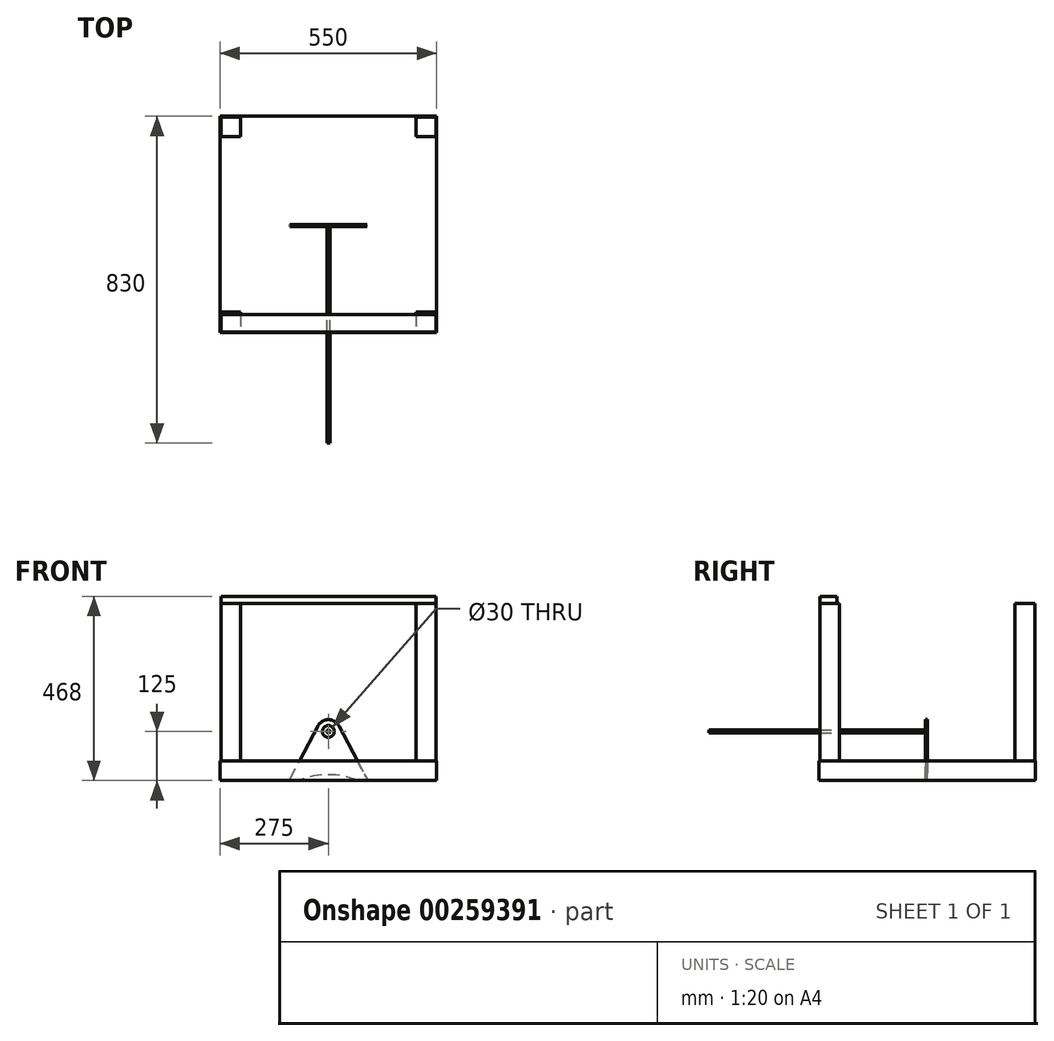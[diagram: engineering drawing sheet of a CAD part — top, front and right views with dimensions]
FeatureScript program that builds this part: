
annotation { "Feature Type Name" : "Feature", "Feature Type Description" : "" }
export const myFeature = defineFeature(function(context is Context, id is Id, definition is map)
    precondition{}
    {
        {
            var Q0;
            Q0=qCreatedBy(makeId("Top.planeOp"),FACE);
            var sketch = newSketch(context, id + "F0", { "sketchPlane" : qUnion([Q0])});
            skLineSegment(sketch, "E0.bottom", {"start": v(-275, 275) * mm, "end": v(275, 275) * mm});
            skLineSegment(sketch, "E0.top", {"start": v(-275, -275) * mm, "end": v(275, -275) * mm});
            skLineSegment(sketch, "E0.left", {"start": v(-275, 275) * mm, "end": v(-275, -275) * mm});
            skLineSegment(sketch, "E0.right", {"start": v(275, 275) * mm, "end": v(275, -275) * mm});
            skLineSegment(sketch, "E1.bottom", {"start": v(-273, -223) * mm, "end": v(-223, -223) * mm});
            skLineSegment(sketch, "E1.top", {"start": v(-273, -273) * mm, "end": v(-223, -273) * mm});
            skLineSegment(sketch, "E1.left", {"start": v(-273, -223) * mm, "end": v(-273, -273) * mm});
            skLineSegment(sketch, "E1.right", {"start": v(-223, -223) * mm, "end": v(-223, -273) * mm});
            skLineSegment(sketch, "E2.bottom", {"start": v(-273, 273) * mm, "end": v(-223, 273) * mm});
            skLineSegment(sketch, "E2.top", {"start": v(-273, 223) * mm, "end": v(-223, 223) * mm});
            skLineSegment(sketch, "E2.left", {"start": v(-273, 273) * mm, "end": v(-273, 223) * mm});
            skLineSegment(sketch, "E2.right", {"start": v(-223, 273) * mm, "end": v(-223, 223) * mm});
            skLineSegment(sketch, "E3.bottom", {"start": v(223, 273) * mm, "end": v(273, 273) * mm});
            skLineSegment(sketch, "E3.top", {"start": v(223, 223) * mm, "end": v(273, 223) * mm});
            skLineSegment(sketch, "E3.left", {"start": v(223, 273) * mm, "end": v(223, 223) * mm});
            skLineSegment(sketch, "E3.right", {"start": v(273, 273) * mm, "end": v(273, 223) * mm});
            skLineSegment(sketch, "E4.bottom", {"start": v(223, -223) * mm, "end": v(273, -223) * mm});
            skLineSegment(sketch, "E4.top", {"start": v(223, -273) * mm, "end": v(273, -273) * mm});
            skLineSegment(sketch, "E4.left", {"start": v(223, -223) * mm, "end": v(223, -273) * mm});
            skLineSegment(sketch, "E4.right", {"start": v(273, -223) * mm, "end": v(273, -273) * mm});
            skSolve(sketch);
        }
        {
            var Q0;
            Q0 = qSketchRegion(id + "F0", true);
            extrude(context, id + "F1", {"entities" : qUnion([Q0]), "depth" : 50 * mm});
        }
        {
            var Q0;
            Q0=makeQuery(id+"F0.imprint","IMPRINT",FACE,{"disambiguationData":[TD([[makeQuery(id+"F0.imprint","IMPRINT",EDGE,{"derivedFrom":sQuery(id+"F0.wireOp",EDGE,"E2.bottom")}),-1.0]])]});
            var Q1;
            Q1=makeQuery(id+"F0.imprint","IMPRINT",FACE,{"disambiguationData":[TD([[makeQuery(id+"F0.imprint","IMPRINT",EDGE,{"derivedFrom":sQuery(id+"F0.wireOp",EDGE,"E3.bottom")}),-1.0]])]});
            var Q2;
            Q2=makeQuery(id+"F0.imprint","IMPRINT",FACE,{"disambiguationData":[TD([[makeQuery(id+"F0.imprint","IMPRINT",EDGE,{"derivedFrom":sQuery(id+"F0.wireOp",EDGE,"E4.bottom")}),-1.0]])]});
            var Q3;
            Q3=makeQuery(id+"F0.imprint","IMPRINT",FACE,{"disambiguationData":[TD([[makeQuery(id+"F0.imprint","IMPRINT",EDGE,{"derivedFrom":sQuery(id+"F0.wireOp",EDGE,"E1.bottom")}),-1.0]])]});
            extrude(context, id + "F2", {"entities" : qUnion([Q0, Q1, Q2, Q3]), "operationType" : NewBodyOperationType.ADD, "depth" : 450 * mm});
        }
        {
            var Q0;
            Q0=makeQuery(id+"F2.opExtrude","SWEPT_FACE",FACE,{"disambiguationData":[OSD([sQuery(id+"F0.wireOp",EDGE,"E4.right")])]});
            var sketch = newSketch(context, id + "F3", { "sketchPlane" : qUnion([Q0])});
            skLineSegment(sketch, "E5.bottom", {"start": v(-273, 450) * mm, "end": v(-229, 450) * mm});
            skLineSegment(sketch, "E5.top", {"start": v(-273, 468) * mm, "end": v(-229, 468) * mm});
            skLineSegment(sketch, "E5.left", {"start": v(-273, 450) * mm, "end": v(-273, 468) * mm});
            skLineSegment(sketch, "E5.right", {"start": v(-229, 450) * mm, "end": v(-229, 468) * mm});
            skSolve(sketch);
        }
        {
            var Q0;
            Q0 = qSketchRegion(id + "F3", true);
            extrude(context, id + "F4", {"entities" : qUnion([Q0]), "oppositeDirection" : true, "depth" : 546 * mm});
        }
        {
            var Q0;
            Q0=qCreatedBy(makeId("Front.planeOp"),FACE);
            var sketch = newSketch(context, id + "F5", { "sketchPlane" : qUnion([Q0])});
            skLineSegment(sketch, "E6", {"start": v(-97.67, 4.4) * mm, "end": v(-26.52, 139.02) * mm});
            skLineSegment(sketch, "E7", {"start": v(26.52, 139.02) * mm, "end": v(97.67, 4.4) * mm});
            skLineSegment(sketch, "E8", {"start": v(95.02, 0) * mm, "end": v(76.97, 0) * mm});
            skArc(sketch, "E9", {"start": v(73.22, 0.73) * mm, "mid": v(0, 15) * mm, "end": v(-73.22, 0.73) * mm});
            skPoint(sketch, "E9.centerSnap0", {"position": v(0, 0) * mm});
            skPoint(sketch, "E10", {"position": v(-75, 0) * mm});
            skPoint(sketch, "E11", {"position": v(75, 0) * mm});
            skLineSegment(sketch, "E12.trimOffspring", {"start": v(-76.97, 0) * mm, "end": v(-95.02, 0) * mm});
            skPoint(sketch, "E13.visualSharp", {"position": v(-100, 0) * mm});
            skArc(sketch, "E13.filletArc", {"start": v(-97.67, 4.4) * mm, "mid": v(-97.6, 1.45) * mm, "end": v(-95.02, 0) * mm});
            skPoint(sketch, "E14.visualSharp", {"position": v(100, 0) * mm});
            skArc(sketch, "E14.filletArc", {"start": v(95.02, 0) * mm, "mid": v(97.6, 1.45) * mm, "end": v(97.67, 4.4) * mm});
            skCircle(sketch, "E15", {"center": v(0, 125) * mm, "radius": 15 * mm});
            skArc(sketch, "E16", {"start": v(26.52, 139.02) * mm, "mid": v(0, 155) * mm, "end": v(-26.52, 139.02) * mm});
            skPoint(sketch, "E17.orphan", {"position": v(0, 189.2) * mm});
            skArc(sketch, "E18.filletArc", {"start": v(-76.97, 0) * mm, "mid": v(-75.06, 0.18) * mm, "end": v(-73.22, 0.73) * mm});
            skArc(sketch, "E19.filletArc", {"start": v(73.22, 0.73) * mm, "mid": v(75.06, 0.18) * mm, "end": v(76.97, 0) * mm});
            skSolve(sketch);
        }
        {
            var Q0;
            Q0 = qSketchRegion(id + "F5", true);
            extrude(context, id + "F6", {"entities" : qUnion([Q0]), "depth" : 5 * mm});
        }
        {
            var Q0;
            Q0=makeQuery(id+"F6.opExtrude","CAP_FACE",FACE,{"disambiguationData":[OSD([sQuery(id+"F5.wireOp",EDGE,"E6"),sQuery(id+"F5.wireOp",EDGE,"E7"),sQuery(id+"F5.wireOp",EDGE,"E8"),sQuery(id+"F5.wireOp",EDGE,"E9"),sQuery(id+"F5.wireOp",EDGE,"E12.trimOffspring"),sQuery(id+"F5.wireOp",EDGE,"E13.filletArc"),sQuery(id+"F5.wireOp",EDGE,"E14.filletArc"),sQuery(id+"F5.wireOp",EDGE,"E15"),sQuery(id+"F5.wireOp",EDGE,"E16"),sQuery(id+"F5.wireOp",EDGE,"E18.filletArc"),sQuery(id+"F5.wireOp",EDGE,"E19.filletArc")])],"isStart":false});
            var sketch = newSketch(context, id + "F7", { "sketchPlane" : qUnion([Q0])});
            skCircle(sketch, "E20", {"center": v(0, 125) * mm, "radius": 4 * mm});
            skSolve(sketch);
        }
        {
            var Q0;
            Q0 = qSketchRegion(id + "F7", true);
            extrude(context, id + "F8", {"entities" : qUnion([Q0]), "depth" : 550 * mm});
        }
    });
